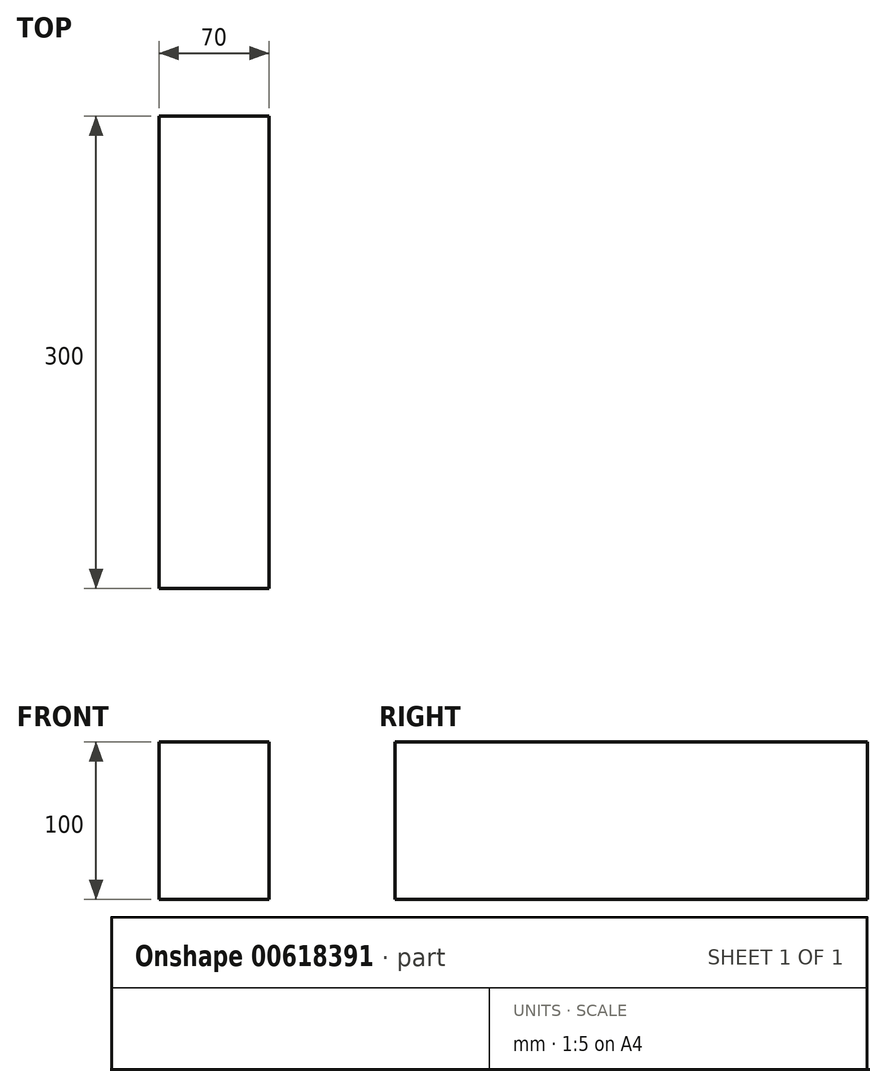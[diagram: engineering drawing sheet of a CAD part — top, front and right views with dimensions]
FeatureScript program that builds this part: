
annotation { "Feature Type Name" : "Feature", "Feature Type Description" : "" }
export const myFeature = defineFeature(function(context is Context, id is Id, definition is map)
    precondition{}
    {
        {
            var Q0;
            Q0=qCreatedBy(makeId("Top.planeOp"),FACE);
            var sketch = newSketch(context, id + "F0", { "sketchPlane" : qUnion([Q0])});
            skLineSegment(sketch, "E0.bottom", {"start": v(0, 0) * mm, "end": v(70, 0) * mm});
            skLineSegment(sketch, "E0.top", {"start": v(0, 300) * mm, "end": v(70, 300) * mm});
            skLineSegment(sketch, "E0.left", {"start": v(0, 0) * mm, "end": v(0, 300) * mm});
            skLineSegment(sketch, "E0.right", {"start": v(70, 0) * mm, "end": v(70, 300) * mm});
            skSolve(sketch);
        }
        {
            var Q0;
            Q0=makeQuery(id+"F0.imprint","IMPRINT",FACE,{"disambiguationData":[TD([[makeQuery(id+"F0.imprint","IMPRINT",EDGE,{"derivedFrom":sQuery(id+"F0.wireOp",EDGE,"E0.bottom")}),1.0]])]});
            extrude(context, id + "F1", {"entities" : qUnion([Q0]), "depth" : 100 * mm, "offsetDistance" : 25 * mm});
        }
    });
